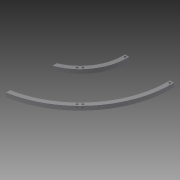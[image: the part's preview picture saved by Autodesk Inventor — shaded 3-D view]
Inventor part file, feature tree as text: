
AUTODESK INVENTOR PART (.ipt)
format: ipt  version: 2013 (Build 170138000, 138)  size: 120,320 bytes
history: native  units: in
note: dims shown in document units (in); Inventor stores cm internally (conversion verified against a paired STEP export)
features: extrude x2, sketch x2, projected_geometry x1
ambient origin geometry x8: Origin, YZ Plane, XZ Plane, XY Plane, X Axis, Y Axis, Z Axis, Center Point
bodies: Solid1 (feature_tree)
feature tree (5):
  extrude  "Extrusion1"  Depth=0.5in TaperAngle=0.0deg
  extrude  "Extrusion2"  Depth=0.266in
  sketch  "Sketch1"  dims[d0=2.0in d1=0.5in d2=0.0in]
  sketch  "Sketch2"  dims[d3=0.266in d4=0.266in d5=0.266in d6=0.266in d7=0.266in d8=0.266in d9=0.5in d10=0.0in]
  projected_geometry  "Projected Loop1"
